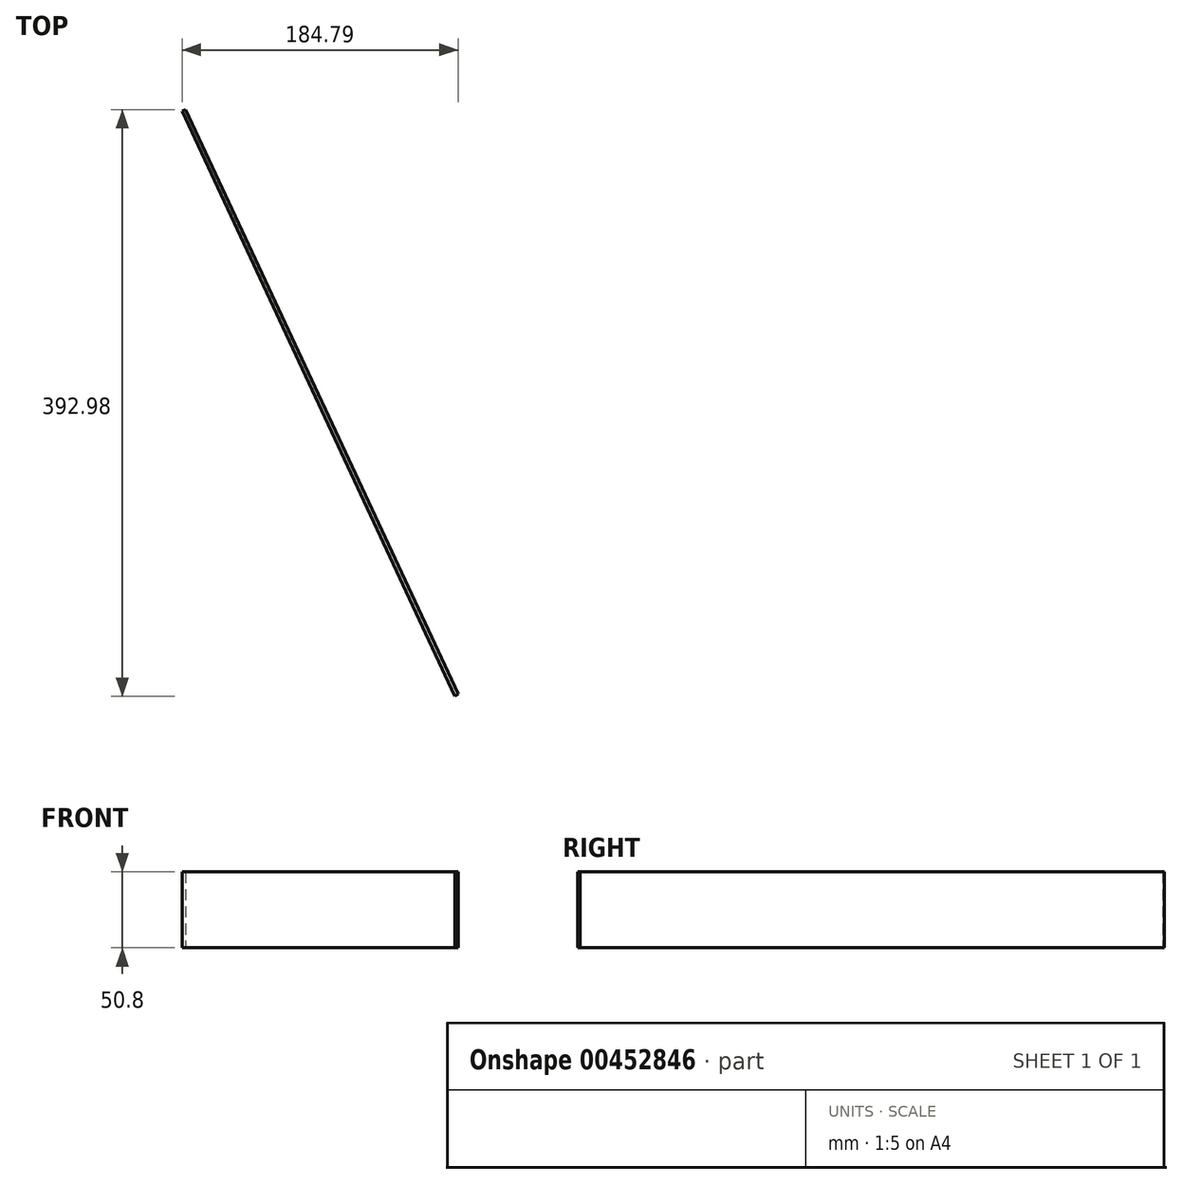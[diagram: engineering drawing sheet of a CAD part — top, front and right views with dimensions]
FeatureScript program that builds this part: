
annotation { "Feature Type Name" : "Feature", "Feature Type Description" : "" }
export const myFeature = defineFeature(function(context is Context, id is Id, definition is map)
    precondition{}
    {
        {
            var Q0;
            Q0=qCreatedBy(makeId("Top.planeOp"),FACE);
            var sketch = newSketch(context, id + "F0", { "sketchPlane" : qUnion([Q0])});
            skLineSegment(sketch, "E0", {"start": v(-200.61, -68.61) * mm, "end": v(-383.1, 322.73) * mm});
            skLineSegment(sketch, "E1", {"start": v(-383.1, 322.73) * mm, "end": v(-385.4, 321.66) * mm});
            skLineSegment(sketch, "E2", {"start": v(-385.4, 321.66) * mm, "end": v(-202.65, -70.25) * mm});
            skLineSegment(sketch, "E3", {"start": v(-202.65, -70.25) * mm, "end": v(-200.61, -68.61) * mm});
            skLineSegment(sketch, "E4", {"start": v(-86.31, -71.15) * mm, "end": v(-86.31, -68.61) * mm});
            skSolve(sketch);
        }
        {
            var Q0;
            Q0=makeQuery(id+"F0.imprint","IMPRINT",FACE,{"disambiguationData":[TD([[makeQuery(id+"F0.imprint","IMPRINT",EDGE,{"derivedFrom":sQuery(id+"F0.wireOp",EDGE,"E0")}),1.0]])]});
            extrude(context, id + "F1", {"entities" : qUnion([Q0]), "depth" : 50.8 * mm});
        }
    });
